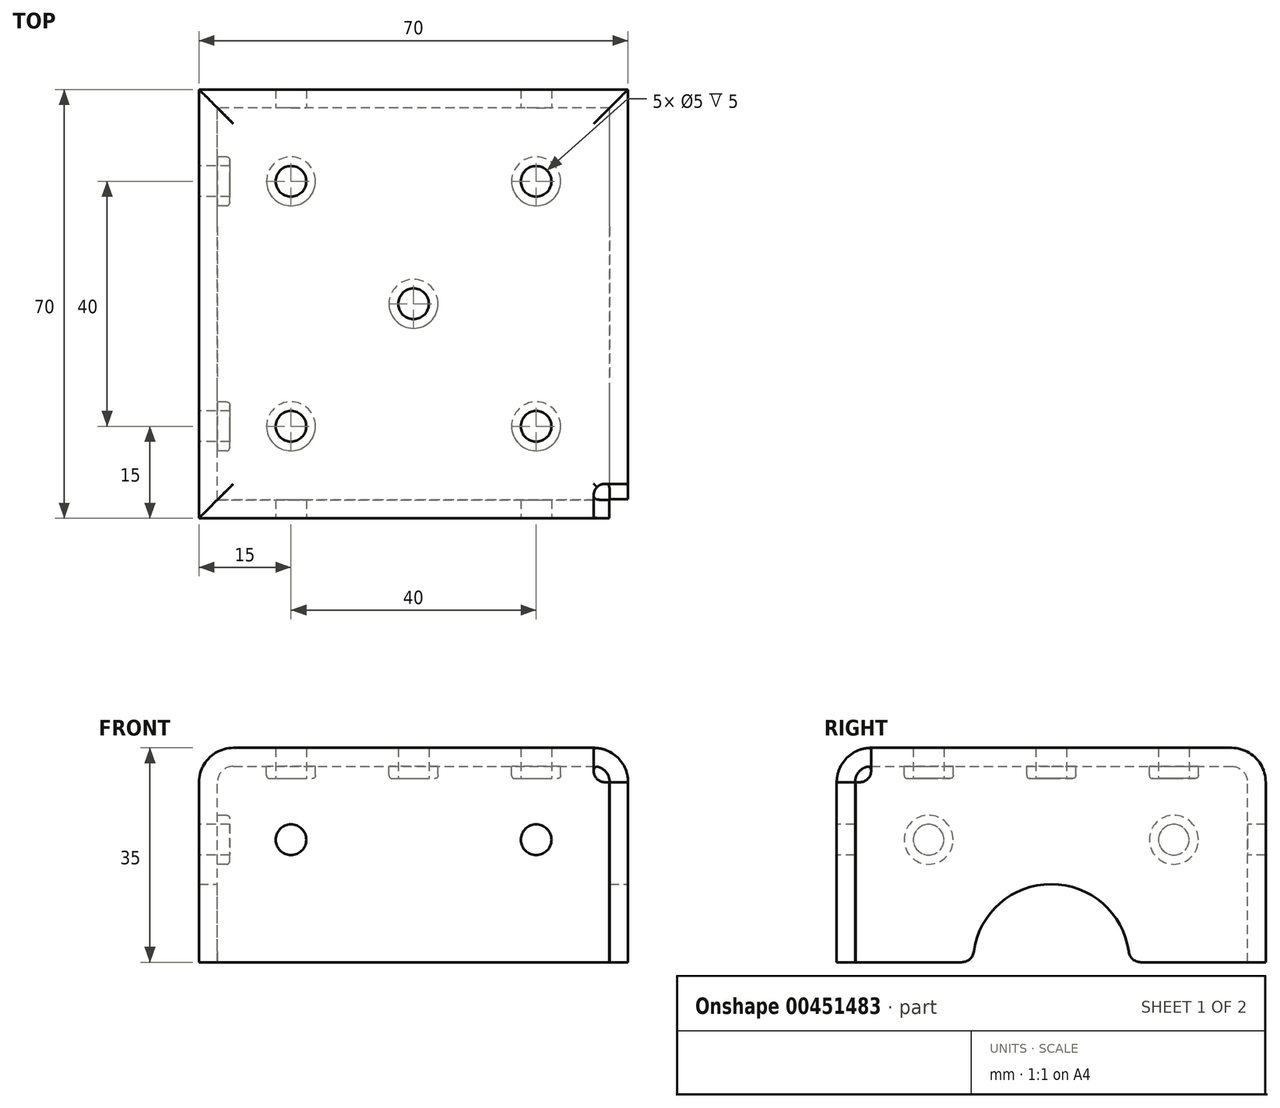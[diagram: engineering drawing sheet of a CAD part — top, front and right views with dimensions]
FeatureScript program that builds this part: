
annotation { "Feature Type Name" : "Feature", "Feature Type Description" : "" }
export const myFeature = defineFeature(function(context is Context, id is Id, definition is map)
    precondition{}
    {
        {
            var Q0;
            Q0=qCreatedBy(makeId("Top.planeOp"),FACE);
            var sketch = newSketch(context, id + "F0", { "sketchPlane" : qUnion([Q0])});
            skLineSegment(sketch, "E0.bottom", {"start": v(35, -35) * mm, "end": v(-35, -35) * mm});
            skLineSegment(sketch, "E0.top", {"start": v(35, 35) * mm, "end": v(-35, 35) * mm});
            skLineSegment(sketch, "E0.left", {"start": v(35, -35) * mm, "end": v(35, 35) * mm});
            skLineSegment(sketch, "E0.right", {"start": v(-35, -35) * mm, "end": v(-35, 35) * mm});
            skPoint(sketch, "E0.middle", {"position": v(0, 0) * mm});
            skSolve(sketch);
        }
        {
            var Q0;
            Q0=qSketchRegion(id+"F0",true);
            extrude(context, id + "F1", {"entities" : qUnion([Q0]), "oppositeDirection" : true, "depth" : 35 * mm});
        }
        {
            var Q0;
            Q0=makeQuery(id+"F1.opExtrude","CAP_EDGE",EDGE,{"disambiguationData":[OSD([sQuery(id+"F0.wireOp",EDGE,"E0.bottom")])],"isStart":true});
            var Q1;
            Q1=makeQuery(id+"F1.opExtrude","CAP_EDGE",EDGE,{"disambiguationData":[OSD([sQuery(id+"F0.wireOp",EDGE,"E0.left")])],"isStart":true});
            var Q2;
            Q2=makeQuery(id+"F1.opExtrude","CAP_EDGE",EDGE,{"disambiguationData":[OSD([sQuery(id+"F0.wireOp",EDGE,"E0.top")])],"isStart":true});
            var Q3;
            Q3=makeQuery(id+"F1.opExtrude","CAP_EDGE",EDGE,{"disambiguationData":[OSD([sQuery(id+"F0.wireOp",EDGE,"E0.right")])],"isStart":true});
            fillet(context, id + "F2", {"entities" : qUnion([Q0, Q1, Q2, Q3]), "radius" : 5.6 * mm, "tangentPropagation" : true, "allowEdgeOverflow" : false});
        }
        {
            var Q0;
            Q0=makeQuery(id+"F1.opExtrude","CAP_FACE",FACE,{"disambiguationData":[OSD([sQuery(id+"F0.wireOp",EDGE,"E0.bottom"),sQuery(id+"F0.wireOp",EDGE,"E0.top"),sQuery(id+"F0.wireOp",EDGE,"E0.left"),sQuery(id+"F0.wireOp",EDGE,"E0.right")])],"isStart":false});
            shell(context, id + "F3", {"entities" : qUnion([Q0]), "thickness" : 3 * mm});
        }
        {
            var Q0;
            Q0=makeQuery(id+"F1.opExtrude","CAP_FACE",FACE,{"disambiguationData":[OSD([sQuery(id+"F0.wireOp",EDGE,"E0.bottom"),sQuery(id+"F0.wireOp",EDGE,"E0.top"),sQuery(id+"F0.wireOp",EDGE,"E0.left"),sQuery(id+"F0.wireOp",EDGE,"E0.right")])],"isStart":false});
            var sketch = newSketch(context, id + "F4", { "sketchPlane" : qUnion([Q0])});
            skLineSegment(sketch, "E1.bottom", {"start": v(35, 35) * mm, "end": v(31.9, 35) * mm});
            skLineSegment(sketch, "E1.top", {"start": v(35, 31.9) * mm, "end": v(31.9, 31.9) * mm});
            skLineSegment(sketch, "E1.left", {"start": v(35, 35) * mm, "end": v(35, 31.9) * mm});
            skLineSegment(sketch, "E1.right", {"start": v(31.9, 35) * mm, "end": v(31.9, 31.9) * mm});
            skSolve(sketch);
        }
        {
            var Q0;
            Q0=qSketchRegion(id+"F4",true);
            extrude(context, id + "F5", {"entities" : qUnion([Q0]), "operationType" : NewBodyOperationType.REMOVE, "oppositeDirection" : true, "depth" : 38.4 * mm});
        }
        {
            var Q0;
            Q0=makeQuery(id+"F1.opExtrude","CAP_FACE",FACE,{"disambiguationData":[OSD([sQuery(id+"F0.wireOp",EDGE,"E0.bottom"),sQuery(id+"F0.wireOp",EDGE,"E0.top"),sQuery(id+"F0.wireOp",EDGE,"E0.left"),sQuery(id+"F0.wireOp",EDGE,"E0.right")])],"isStart":true});
            var sketch = newSketch(context, id + "F6", { "sketchPlane" : qUnion([Q0])});
            skLineSegment(sketch, "E2.bottom", {"start": v(29.4, -29.4) * mm, "end": v(35, -29.4) * mm});
            skLineSegment(sketch, "E2.top", {"start": v(29.4, -35) * mm, "end": v(35, -35) * mm});
            skLineSegment(sketch, "E2.left", {"start": v(29.4, -29.4) * mm, "end": v(29.4, -35) * mm});
            skLineSegment(sketch, "E2.right", {"start": v(35, -29.4) * mm, "end": v(35, -35) * mm});
            skSolve(sketch);
        }
        {
            var Q0;
            Q0=makeQuery(id+"F6.imprint","IMPRINT",FACE,{"disambiguationData":[TD([[makeQuery(id+"F6.imprint","IMPRINT",EDGE,{"derivedFrom":sQuery(id+"F6.wireOp",EDGE,"E2.bottom")}),-1.0]])]});
            extrude(context, id + "F7", {"entities" : qUnion([Q0]), "operationType" : NewBodyOperationType.REMOVE, "oppositeDirection" : true, "depth" : 5.6 * mm});
        }
        {
            var Q0;
            Q0=makeQuery(id+"F7.boolean.opBoolean","COPY",EDGE,{"derivedFrom":makeQuery(id+"F7.opExtrude","SWEPT_EDGE",EDGE,{"disambiguationData":[OSD([sQuery(id+"F0.wireOp",EDGE,"E0.bottom"),sQuery(id+"F0.wireOp",EDGE,"E0.top"),sQuery(id+"F0.wireOp",EDGE,"E0.left"),sQuery(id+"F0.wireOp",EDGE,"E0.right"),sQuery(id+"F6.wireOp",EDGE,"E2.bottom"),sQuery(id+"F6.wireOp",EDGE,"E2.left")])]})});
            var Q1;
            Q1=makeQuery(id+"F7.boolean.opBoolean","COPY",EDGE,{"derivedFrom":makeQuery(id+"F7.opExtrude","CAP_EDGE",EDGE,{"disambiguationData":[OSD([sQuery(id+"F6.wireOp",EDGE,"E2.bottom")])],"isStart":false})});
            var Q2;
            Q2=makeQuery(id+"F7.boolean.opBoolean","COPY",EDGE,{"derivedFrom":makeQuery(id+"F7.opExtrude","CAP_EDGE",EDGE,{"disambiguationData":[OSD([sQuery(id+"F6.wireOp",EDGE,"E2.left")])],"isStart":false})});
            fillet(context, id + "F8", {"entities" : qUnion([Q0, Q1, Q2]), "radius" : 1.8 * mm, "tangentPropagation" : true, "allowEdgeOverflow" : false});
        }
        {
            var Q0;
            Q0=makeQuery(id+"F3.opShell","OFFSET_FACE",FACE,{"disambiguationData":[OSD([sQuery(id+"F0.wireOp",EDGE,"E0.bottom"),sQuery(id+"F0.wireOp",EDGE,"E0.top"),sQuery(id+"F0.wireOp",EDGE,"E0.left"),sQuery(id+"F0.wireOp",EDGE,"E0.right")])]});
            var sketch = newSketch(context, id + "F9", { "sketchPlane" : qUnion([Q0])});
            skCircle(sketch, "E3", {"center": v(-20, 20) * mm, "radius": 4 * mm});
            skLineSegment(sketch, "E4.bottom", {"start": v(-20, 20) * mm, "end": v(20, 20) * mm, "construction": true});
            skLineSegment(sketch, "E4.top", {"start": v(-20, -20) * mm, "end": v(20, -20) * mm, "construction": true});
            skLineSegment(sketch, "E4.left", {"start": v(-20, 20) * mm, "end": v(-20, -20) * mm, "construction": true});
            skLineSegment(sketch, "E4.right", {"start": v(20, 20) * mm, "end": v(20, -20) * mm, "construction": true});
            skPoint(sketch, "E4.middle", {"position": v(0, 0) * mm});
            skCircle(sketch, "E5", {"center": v(-20, -20) * mm, "radius": 4 * mm});
            skCircle(sketch, "E6", {"center": v(20, -20) * mm, "radius": 4 * mm});
            skCircle(sketch, "E7", {"center": v(20, 20) * mm, "radius": 4 * mm});
            skCircle(sketch, "E8", {"center": v(0, 0) * mm, "radius": 4 * mm});
            skSolve(sketch);
        }
        {
            var Q0;
            Q0=makeQuery(id+"F9.imprint","IMPRINT",FACE,{"disambiguationData":[TD([[makeQuery(id+"F9.imprint","IMPRINT",EDGE,{"derivedFrom":sQuery(id+"F9.wireOp",EDGE,"E5")}),1.0]])]});
            var Q1;
            Q1=makeQuery(id+"F9.imprint","IMPRINT",FACE,{"disambiguationData":[TD([[makeQuery(id+"F9.imprint","IMPRINT",EDGE,{"derivedFrom":sQuery(id+"F9.wireOp",EDGE,"E6")}),1.0]])]});
            var Q2;
            Q2=makeQuery(id+"F9.imprint","IMPRINT",FACE,{"disambiguationData":[TD([[makeQuery(id+"F9.imprint","IMPRINT",EDGE,{"derivedFrom":sQuery(id+"F9.wireOp",EDGE,"E7")}),1.0]])]});
            var Q3;
            Q3=makeQuery(id+"F9.imprint","IMPRINT",FACE,{"disambiguationData":[TD([[makeQuery(id+"F9.imprint","IMPRINT",EDGE,{"derivedFrom":sQuery(id+"F9.wireOp",EDGE,"E3")}),1.0]])]});
            var Q4;
            Q4=makeQuery(id+"F9.imprint","IMPRINT",FACE,{"disambiguationData":[TD([[makeQuery(id+"F9.imprint","IMPRINT",EDGE,{"derivedFrom":sQuery(id+"F9.wireOp",EDGE,"E8")}),1.0]])]});
            extrude(context, id + "F10", {"entities" : qUnion([Q0, Q1, Q2, Q3, Q4]), "operationType" : NewBodyOperationType.ADD, "depth" : 2 * mm});
        }
        {
            var Q0;
            Q0=makeQuery(id+"F10.opExtrude","CAP_EDGE",EDGE,{"disambiguationData":[OSD([sQuery(id+"F9.wireOp",EDGE,"E3")])],"isStart":false});
            var Q1;
            Q1=makeQuery(id+"F10.opExtrude","CAP_EDGE",EDGE,{"disambiguationData":[OSD([sQuery(id+"F9.wireOp",EDGE,"E3")])],"isStart":true});
            var Q2;
            Q2=makeQuery(id+"F10.opExtrude","CAP_FACE",FACE,{"disambiguationData":[OSD([sQuery(id+"F9.wireOp",EDGE,"E5")])],"isStart":false});
            var Q3;
            Q3=makeQuery(id+"F10.opExtrude","CAP_FACE",FACE,{"disambiguationData":[OSD([sQuery(id+"F9.wireOp",EDGE,"E6")])],"isStart":false});
            var Q4;
            Q4=makeQuery(id+"F10.opExtrude","CAP_FACE",FACE,{"disambiguationData":[OSD([sQuery(id+"F9.wireOp",EDGE,"E7")])],"isStart":false});
            var Q5;
            Q5=makeQuery(id+"F10.opExtrude","CAP_EDGE",EDGE,{"disambiguationData":[OSD([sQuery(id+"F9.wireOp",EDGE,"E5")])],"isStart":true});
            var Q6;
            Q6=makeQuery(id+"F10.opExtrude","CAP_EDGE",EDGE,{"disambiguationData":[OSD([sQuery(id+"F9.wireOp",EDGE,"E6")])],"isStart":true});
            var Q7;
            Q7=makeQuery(id+"F10.opExtrude","CAP_EDGE",EDGE,{"disambiguationData":[OSD([sQuery(id+"F9.wireOp",EDGE,"E7")])],"isStart":true});
            var Q8;
            Q8=makeQuery(id+"F10.opExtrude","CAP_EDGE",EDGE,{"disambiguationData":[OSD([sQuery(id+"F9.wireOp",EDGE,"E8")])],"isStart":true});
            var Q9;
            Q9=makeQuery(id+"F10.opExtrude","CAP_EDGE",EDGE,{"disambiguationData":[OSD([sQuery(id+"F9.wireOp",EDGE,"E8")])],"isStart":false});
            fillet(context, id + "F11", {"entities" : qUnion([Q0, Q1, Q2, Q3, Q4, Q5, Q6, Q7, Q8, Q9]), "radius" : 0.5 * mm, "tangentPropagation" : true, "allowEdgeOverflow" : false});
        }
        {
            var Q0;
            Q0=makeQuery(id+"F1.opExtrude","CAP_FACE",FACE,{"disambiguationData":[OSD([sQuery(id+"F0.wireOp",EDGE,"E0.bottom"),sQuery(id+"F0.wireOp",EDGE,"E0.top"),sQuery(id+"F0.wireOp",EDGE,"E0.left"),sQuery(id+"F0.wireOp",EDGE,"E0.right")])],"isStart":true});
            var sketch = newSketch(context, id + "F12", { "sketchPlane" : qUnion([Q0])});
            skCircle(sketch, "E9.0", {"center": v(-20, -20) * mm, "radius": 3.5 * mm, "construction": true});
            skCircle(sketch, "E10.0", {"center": v(-20, 20) * mm, "radius": 3.5 * mm, "construction": true});
            skCircle(sketch, "E11.0", {"center": v(20, 20) * mm, "radius": 3.5 * mm, "construction": true});
            skCircle(sketch, "E12.0", {"center": v(20, -20) * mm, "radius": 3.5 * mm, "construction": true});
            skCircle(sketch, "E13.0", {"center": v(0, 0) * mm, "radius": 3.5 * mm, "construction": true});
            skSolve(sketch);
        }
        {
            var Q0;
            Q0=sQuery(id+"F12.wireOp",VERTEX,"E9.0.center");
            var Q1;
            Q1=sQuery(id+"F12.wireOp",VERTEX,"E10.0.center");
            var Q2;
            Q2=sQuery(id+"F12.wireOp",VERTEX,"E11.0.center");
            var Q3;
            Q3=sQuery(id+"F12.wireOp",VERTEX,"E13.0.center");
            var Q4;
            Q4=sQuery(id+"F12.wireOp",VERTEX,"E12.0.center");
            var Q5;
            Q5=makeQuery(id+"F1.opExtrude","SWEPT_BODY",BODY,{"disambiguationData":[OSD([sQuery(id+"F0.wireOp",EDGE,"E0.bottom"),sQuery(id+"F0.wireOp",EDGE,"E0.top"),sQuery(id+"F0.wireOp",EDGE,"E0.left"),sQuery(id+"F0.wireOp",EDGE,"E0.right")])]});
            hole(context, id + "F13", {"style" : HoleStyle.SIMPLE, "endStyle" : HoleEndStyle.THROUGH, "standardTappedOrClearance" : lookupTablePath({ "standard" : "ISO", "engagement" : "75%", "pitch" : "1 mm", "size" : "M6", "type" : "Tapped" }), "standardBlindInLast" : lookupTablePath({ "standard" : "ISO", "engagement" : "75%", "pitch" : "1 mm", "size" : "M6", "type" : "Tapped" }), "holeDiameter" : 5 * mm, "locations" : qUnion([Q0, Q1, Q2, Q3, Q4]), "scope" : qUnion([Q5]), "isTappedThrough" : true, "majorDiameter" : 6 * mm, "showTappedDepth" : true, "startStyle" : HoleStartStyle.PART});
        }
        {
            var Q0;
            {var subQ0=sQuery(id+"F0.wireOp",EDGE,"E0.right");Q0=makeQuery(id+"F3.opShell","OFFSET_FACE",FACE,{"disambiguationData":[OSD([subQ0]),TDD([makeQuery(id+"F1.opExtrude","SWEPT_FACE",FACE,{"disambiguationData":[OSD([subQ0])]})])]});}
            var sketch = newSketch(context, id + "F14", { "sketchPlane" : qUnion([Q0])});
            skCircle(sketch, "E14", {"center": v(-20, -15) * mm, "radius": 4 * mm});
            skCircle(sketch, "E15", {"center": v(20, -15) * mm, "radius": 4 * mm});
            skSolve(sketch);
        }
        {
            var Q0;
            Q0=qSketchRegion(id+"F14",true);
            extrude(context, id + "F15", {"entities" : qUnion([Q0]), "operationType" : NewBodyOperationType.ADD, "depth" : 2 * mm});
        }
        {
            var Q0;
            Q0=makeQuery(id+"F15.opExtrude","CAP_EDGE",EDGE,{"disambiguationData":[OSD([sQuery(id+"F14.wireOp",EDGE,"E14")])],"isStart":false});
            var Q1;
            Q1=makeQuery(id+"F15.opExtrude","CAP_EDGE",EDGE,{"disambiguationData":[OSD([sQuery(id+"F14.wireOp",EDGE,"E15")])],"isStart":false});
            var Q2;
            Q2=makeQuery(id+"F15.opExtrude","CAP_EDGE",EDGE,{"disambiguationData":[OSD([sQuery(id+"F14.wireOp",EDGE,"E15")])],"isStart":true});
            var Q3;
            Q3=makeQuery(id+"F15.opExtrude","CAP_EDGE",EDGE,{"disambiguationData":[OSD([sQuery(id+"F14.wireOp",EDGE,"E14")])],"isStart":true});
            fillet(context, id + "F16", {"entities" : qUnion([Q0, Q1, Q2, Q3]), "radius" : 0.5 * mm, "tangentPropagation" : true, "allowEdgeOverflow" : false});
        }
        {
            var Q0;
            Q0=makeQuery(id+"F15.opExtrude","CAP_FACE",FACE,{"disambiguationData":[OSD([sQuery(id+"F14.wireOp",EDGE,"E14")])],"isStart":false});
            var sketch = newSketch(context, id + "F17", { "sketchPlane" : qUnion([Q0])});
            skPoint(sketch, "E16", {"position": v(-20, -15) * mm});
            skPoint(sketch, "E17", {"position": v(20, -15) * mm});
            skSolve(sketch);
        }
        {
            var Q0;
            Q0=sQuery(id+"F17.wireOp",VERTEX,"E16");
            var Q1;
            Q1=sQuery(id+"F17.wireOp",VERTEX,"E17");
            var Q2;
            Q2=makeQuery(id+"F1.opExtrude","SWEPT_BODY",BODY,{"disambiguationData":[OSD([sQuery(id+"F0.wireOp",EDGE,"E0.bottom"),sQuery(id+"F0.wireOp",EDGE,"E0.top"),sQuery(id+"F0.wireOp",EDGE,"E0.left"),sQuery(id+"F0.wireOp",EDGE,"E0.right")])]});
            hole(context, id + "F18", {"style" : HoleStyle.SIMPLE, "endStyle" : HoleEndStyle.THROUGH, "standardTappedOrClearance" : lookupTablePath({ "standard" : "ISO", "engagement" : "75%", "pitch" : "1 mm", "size" : "M6", "type" : "Tapped" }), "standardBlindInLast" : lookupTablePath({ "standard" : "ISO", "engagement" : "75%", "pitch" : "1 mm", "size" : "M6", "type" : "Tapped" }), "holeDiameter" : 5 * mm, "locations" : qUnion([Q0, Q1]), "scope" : qUnion([Q2]), "isTappedThrough" : true, "majorDiameter" : 6 * mm, "showTappedDepth" : true, "startStyle" : HoleStartStyle.PART});
        }
        {
            var Q0;
            Q0=makeQuery(id+"F1.opExtrude","SWEPT_FACE",FACE,{"disambiguationData":[OSD([sQuery(id+"F0.wireOp",EDGE,"E0.top")])]});
            var sketch = newSketch(context, id + "F19", { "sketchPlane" : qUnion([Q0])});
            skPoint(sketch, "E18", {"position": v(-20, -15) * mm});
            skPoint(sketch, "E19", {"position": v(20, -15) * mm});
            skSolve(sketch);
        }
        {
            var Q0;
            Q0=sQuery(id+"F19.wireOp",VERTEX,"E19");
            var Q1;
            Q1=sQuery(id+"F19.wireOp",VERTEX,"E18");
            var Q2;
            Q2=makeQuery(id+"F1.opExtrude","SWEPT_BODY",BODY,{"disambiguationData":[OSD([sQuery(id+"F0.wireOp",EDGE,"E0.bottom"),sQuery(id+"F0.wireOp",EDGE,"E0.top"),sQuery(id+"F0.wireOp",EDGE,"E0.left"),sQuery(id+"F0.wireOp",EDGE,"E0.right")])]});
            hole(context, id + "F20", {"style" : HoleStyle.SIMPLE, "endStyle" : HoleEndStyle.THROUGH, "standardTappedOrClearance" : lookupTablePath({ "standard" : "ISO", "engagement" : "75%", "pitch" : "1 mm", "size" : "M6", "type" : "Tapped" }), "standardBlindInLast" : lookupTablePath({ "standard" : "ISO", "engagement" : "75%", "pitch" : "1 mm", "size" : "M6", "type" : "Tapped" }), "holeDiameter" : 5 * mm, "locations" : qUnion([Q0, Q1]), "scope" : qUnion([Q2]), "isTappedThrough" : true, "majorDiameter" : 6 * mm, "showTappedDepth" : true, "startStyle" : HoleStartStyle.PART});
        }
        {
            var Q0;
            Q0=makeQuery(id+"F1.opExtrude","SWEPT_FACE",FACE,{"disambiguationData":[OSD([sQuery(id+"F0.wireOp",EDGE,"E0.bottom")])]});
            var sketch = newSketch(context, id + "F21", { "sketchPlane" : qUnion([Q0])});
            skCircle(sketch, "E20", {"center": v(0, -35) * mm, "radius": 15.25 * mm});
            skSolve(sketch);
        }
        {
            var Q0;
            {var subQ0=sQuery(id+"F21.wireOp",EDGE,"E20");var subQ1=makeQuery(id+"F1.opExtrude","CAP_EDGE",EDGE,{"disambiguationData":[OSD([sQuery(id+"F0.wireOp",EDGE,"E0.bottom")])],"isStart":false});var subQ2=makeQuery(id+"F21.imprint","INTERSECT",VERTEX,{"disambiguationData":[OD(0.0)],"derivedFrom":[subQ1,subQ0]});Q0=makeQuery(id+"F21.imprint","IMPRINT",FACE,{"disambiguationData":[TD([[makeQuery(id+"F21.imprint","IMPRINT",EDGE,{"disambiguationData":[TD([[subQ2,-1.0]])],"derivedFrom":subQ0}),1.0]])]});}
            extrude(context, id + "F22", {"entities" : qUnion([Q0]), "operationType" : NewBodyOperationType.REMOVE, "endBound" : BoundingType.THROUGH_ALL, "oppositeDirection" : true, "depth" : 25 * mm});
        }
        {
            var Q0;
            Q0=makeQuery(id+"F1.opExtrude","SWEPT_FACE",FACE,{"disambiguationData":[OSD([sQuery(id+"F0.wireOp",EDGE,"E0.left")])]});
            var sketch = newSketch(context, id + "F23", { "sketchPlane" : qUnion([Q0])});
            skCircle(sketch, "E21", {"center": v(0, -35) * mm, "radius": 12.75 * mm});
            skSolve(sketch);
        }
        {
            var Q0;
            Q0=qSketchRegion(id+"F23",true);
            extrude(context, id + "F24", {"entities" : qUnion([Q0]), "operationType" : NewBodyOperationType.REMOVE, "endBound" : BoundingType.THROUGH_ALL, "oppositeDirection" : true, "depth" : 25 * mm});
        }
        {
            var Q0;
            {var subQ0=sQuery(id+"F0.wireOp",EDGE,"E0.bottom");var subQ1=makeQuery(id+"F1.opExtrude","SWEPT_FACE",FACE,{"disambiguationData":[OSD([subQ0])]});var subQ2=sQuery(id+"F21.wireOp",EDGE,"E20");Q0=makeQuery(id+"F22.boolean.opBoolean","COPY",EDGE,{"disambiguationData":[TD([subQ1])],"derivedFrom":makeQuery(id+"F22.opExtrude","SWEPT_EDGE",EDGE,{"disambiguationData":[OSD([subQ0,subQ2]),TDD([makeQuery(id+"F21.imprint","INTERSECT",VERTEX,{"disambiguationData":[OD(0.0)],"derivedFrom":[makeQuery(id+"F1.opExtrude","CAP_EDGE",EDGE,{"disambiguationData":[OSD([subQ0])],"isStart":false}),subQ2]})])]})});}
            var Q1;
            {var subQ0=sQuery(id+"F0.wireOp",EDGE,"E0.bottom");var subQ1=makeQuery(id+"F1.opExtrude","SWEPT_FACE",FACE,{"disambiguationData":[OSD([subQ0])]});var subQ2=sQuery(id+"F21.wireOp",EDGE,"E20");Q1=makeQuery(id+"F22.boolean.opBoolean","COPY",EDGE,{"disambiguationData":[TD([subQ1])],"derivedFrom":makeQuery(id+"F22.opExtrude","SWEPT_EDGE",EDGE,{"disambiguationData":[OSD([subQ0,subQ2]),TDD([makeQuery(id+"F21.imprint","INTERSECT",VERTEX,{"disambiguationData":[OD(1.0)],"derivedFrom":[makeQuery(id+"F1.opExtrude","CAP_EDGE",EDGE,{"disambiguationData":[OSD([subQ0])],"isStart":false}),subQ2]})])]})});}
            var Q2;
            {var subQ0=sQuery(id+"F0.wireOp",EDGE,"E0.right");var subQ1=makeQuery(id+"F1.opExtrude","SWEPT_FACE",FACE,{"disambiguationData":[OSD([subQ0])]});var subQ6=sQuery(id+"F0.wireOp",EDGE,"E0.top");var subQ7=makeQuery(id+"F1.opExtrude","SWEPT_FACE",FACE,{"disambiguationData":[OSD([subQ6])]});var subQ9=sQuery(id+"F0.wireOp",EDGE,"E0.left");Q2=makeQuery(id+"F24.boolean.opBoolean","INTERSECT",EDGE,{"disambiguationData":[OD(0.0)],"derivedFrom":[makeQuery(id+"Fg5Al07xBOhborq_1.1.FdxJJ5X4k0Y0wya_1.1.F5.boolean.opBoolean","SPLIT",FACE,{"disambiguationData":[TD([subQ1])],"derivedFrom":makeQuery(id+"Fg5Al07xBOhborq_1.1.F5.boolean.opBoolean","SPLIT",FACE,{"disambiguationData":[TD([subQ7])],"derivedFrom":makeQuery(id+"FdxJJ5X4k0Y0wya_1.1.F5.boolean.opBoolean","SPLIT",FACE,{"disambiguationData":[TD([subQ7])],"derivedFrom":makeQuery(id+"F1.opExtrude","CAP_FACE",FACE,{"disambiguationData":[OSD([sQuery(id+"F0.wireOp",EDGE,"E0.bottom"),subQ6,subQ9,subQ0])],"isStart":false})})})}),makeQuery(id+"F24.opExtrude","SWEPT_FACE",FACE,{"disambiguationData":[OSD([sQuery(id+"F23.wireOp",EDGE,"E21")])]})]});}
            var Q3;
            {var subQ0=sQuery(id+"F0.wireOp",EDGE,"E0.right");var subQ1=makeQuery(id+"F1.opExtrude","SWEPT_FACE",FACE,{"disambiguationData":[OSD([subQ0])]});var subQ6=sQuery(id+"F0.wireOp",EDGE,"E0.top");var subQ7=makeQuery(id+"F1.opExtrude","SWEPT_FACE",FACE,{"disambiguationData":[OSD([subQ6])]});var subQ9=sQuery(id+"F0.wireOp",EDGE,"E0.left");Q3=makeQuery(id+"F24.boolean.opBoolean","INTERSECT",EDGE,{"disambiguationData":[OD(1.0)],"derivedFrom":[makeQuery(id+"Fg5Al07xBOhborq_1.1.FdxJJ5X4k0Y0wya_1.1.F5.boolean.opBoolean","SPLIT",FACE,{"disambiguationData":[TD([subQ1])],"derivedFrom":makeQuery(id+"Fg5Al07xBOhborq_1.1.F5.boolean.opBoolean","SPLIT",FACE,{"disambiguationData":[TD([subQ7])],"derivedFrom":makeQuery(id+"FdxJJ5X4k0Y0wya_1.1.F5.boolean.opBoolean","SPLIT",FACE,{"disambiguationData":[TD([subQ7])],"derivedFrom":makeQuery(id+"F1.opExtrude","CAP_FACE",FACE,{"disambiguationData":[OSD([sQuery(id+"F0.wireOp",EDGE,"E0.bottom"),subQ6,subQ9,subQ0])],"isStart":false})})})}),makeQuery(id+"F24.opExtrude","SWEPT_FACE",FACE,{"disambiguationData":[OSD([sQuery(id+"F23.wireOp",EDGE,"E21")])]})]});}
            var Q4;
            Q4=makeQuery(id+"Fg5Al07xBOhborq_1.1.FdxJJ5X4k0Y0wya_1.1.F5.boolean.opBoolean","COPY",EDGE,{"derivedFrom":makeQuery(id+"Fg5Al07xBOhborq_1.1.FdxJJ5X4k0Y0wya_1.1.F5.opExtrude","CAP_EDGE",EDGE,{"disambiguationData":[OSD([sQuery(id+"F4.wireOp",EDGE,"E1.top")])],"isStart":true})});
            var Q5;
            Q5=makeQuery(id+"Fg5Al07xBOhborq_1.1.FdxJJ5X4k0Y0wya_1.1.F5.boolean.opBoolean","COPY",EDGE,{"derivedFrom":makeQuery(id+"Fg5Al07xBOhborq_1.1.FdxJJ5X4k0Y0wya_1.1.F5.opExtrude","CAP_EDGE",EDGE,{"disambiguationData":[OSD([sQuery(id+"F4.wireOp",EDGE,"E1.right")])],"isStart":true})});
            var Q6;
            {var subQ0=sQuery(id+"F0.wireOp",EDGE,"E0.top");var subQ1=sQuery(id+"F0.wireOp",EDGE,"E0.bottom");var subQ2=makeQuery(id+"F1.opExtrude","SWEPT_FACE",FACE,{"disambiguationData":[OSD([subQ0])]});var subQ3=sQuery(id+"F21.wireOp",EDGE,"E20");Q6=makeQuery(id+"F22.boolean.opBoolean","COPY",EDGE,{"disambiguationData":[TD([subQ2])],"derivedFrom":makeQuery(id+"F22.opExtrude","SWEPT_EDGE",EDGE,{"disambiguationData":[OSD([subQ1,subQ3]),TDD([makeQuery(id+"F21.imprint","INTERSECT",VERTEX,{"disambiguationData":[OD(1.0)],"derivedFrom":[makeQuery(id+"F1.opExtrude","CAP_EDGE",EDGE,{"disambiguationData":[OSD([subQ1])],"isStart":false}),subQ3]})])]})});}
            var Q7;
            {var subQ0=sQuery(id+"F0.wireOp",EDGE,"E0.top");var subQ1=sQuery(id+"F0.wireOp",EDGE,"E0.bottom");var subQ2=makeQuery(id+"F1.opExtrude","SWEPT_FACE",FACE,{"disambiguationData":[OSD([subQ0])]});var subQ3=sQuery(id+"F21.wireOp",EDGE,"E20");Q7=makeQuery(id+"F22.boolean.opBoolean","COPY",EDGE,{"disambiguationData":[TD([subQ2])],"derivedFrom":makeQuery(id+"F22.opExtrude","SWEPT_EDGE",EDGE,{"disambiguationData":[OSD([subQ1,subQ3]),TDD([makeQuery(id+"F21.imprint","INTERSECT",VERTEX,{"disambiguationData":[OD(0.0)],"derivedFrom":[makeQuery(id+"F1.opExtrude","CAP_EDGE",EDGE,{"disambiguationData":[OSD([subQ1])],"isStart":false}),subQ3]})])]})});}
            var Q8;
            {var subQ0=sQuery(id+"F0.wireOp",EDGE,"E0.left");var subQ1=makeQuery(id+"F1.opExtrude","SWEPT_FACE",FACE,{"disambiguationData":[OSD([subQ0])]});var subQ5=sQuery(id+"F0.wireOp",EDGE,"E0.top");var subQ6=makeQuery(id+"F1.opExtrude","SWEPT_FACE",FACE,{"disambiguationData":[OSD([subQ5])]});var subQ7=sQuery(id+"F0.wireOp",EDGE,"E0.right");Q8=makeQuery(id+"F24.boolean.opBoolean","INTERSECT",EDGE,{"disambiguationData":[OD(1.0)],"derivedFrom":[makeQuery(id+"Fg5Al07xBOhborq_1.1.F5.boolean.opBoolean","SPLIT",FACE,{"disambiguationData":[TD([subQ1])],"derivedFrom":makeQuery(id+"FdxJJ5X4k0Y0wya_1.1.F5.boolean.opBoolean","SPLIT",FACE,{"disambiguationData":[TD([subQ6])],"derivedFrom":makeQuery(id+"F1.opExtrude","CAP_FACE",FACE,{"disambiguationData":[OSD([sQuery(id+"F0.wireOp",EDGE,"E0.bottom"),subQ5,subQ0,subQ7])],"isStart":false})})}),makeQuery(id+"F24.opExtrude","SWEPT_FACE",FACE,{"disambiguationData":[OSD([sQuery(id+"F23.wireOp",EDGE,"E21")])]})]});}
            var Q9;
            {var subQ0=sQuery(id+"F0.wireOp",EDGE,"E0.left");var subQ1=makeQuery(id+"F1.opExtrude","SWEPT_FACE",FACE,{"disambiguationData":[OSD([subQ0])]});var subQ5=sQuery(id+"F0.wireOp",EDGE,"E0.top");var subQ6=makeQuery(id+"F1.opExtrude","SWEPT_FACE",FACE,{"disambiguationData":[OSD([subQ5])]});var subQ7=sQuery(id+"F0.wireOp",EDGE,"E0.right");Q9=makeQuery(id+"F24.boolean.opBoolean","INTERSECT",EDGE,{"disambiguationData":[OD(0.0)],"derivedFrom":[makeQuery(id+"Fg5Al07xBOhborq_1.1.F5.boolean.opBoolean","SPLIT",FACE,{"disambiguationData":[TD([subQ1])],"derivedFrom":makeQuery(id+"FdxJJ5X4k0Y0wya_1.1.F5.boolean.opBoolean","SPLIT",FACE,{"disambiguationData":[TD([subQ6])],"derivedFrom":makeQuery(id+"F1.opExtrude","CAP_FACE",FACE,{"disambiguationData":[OSD([sQuery(id+"F0.wireOp",EDGE,"E0.bottom"),subQ5,subQ0,subQ7])],"isStart":false})})}),makeQuery(id+"F24.opExtrude","SWEPT_FACE",FACE,{"disambiguationData":[OSD([sQuery(id+"F23.wireOp",EDGE,"E21")])]})]});}
            fillet(context, id + "F25", {"entities" : qUnion([Q0, Q1, Q2, Q3, Q4, Q5, Q6, Q7, Q8, Q9]), "radius" : 2 * mm, "tangentPropagation" : true, "allowEdgeOverflow" : false});
        }
    });
